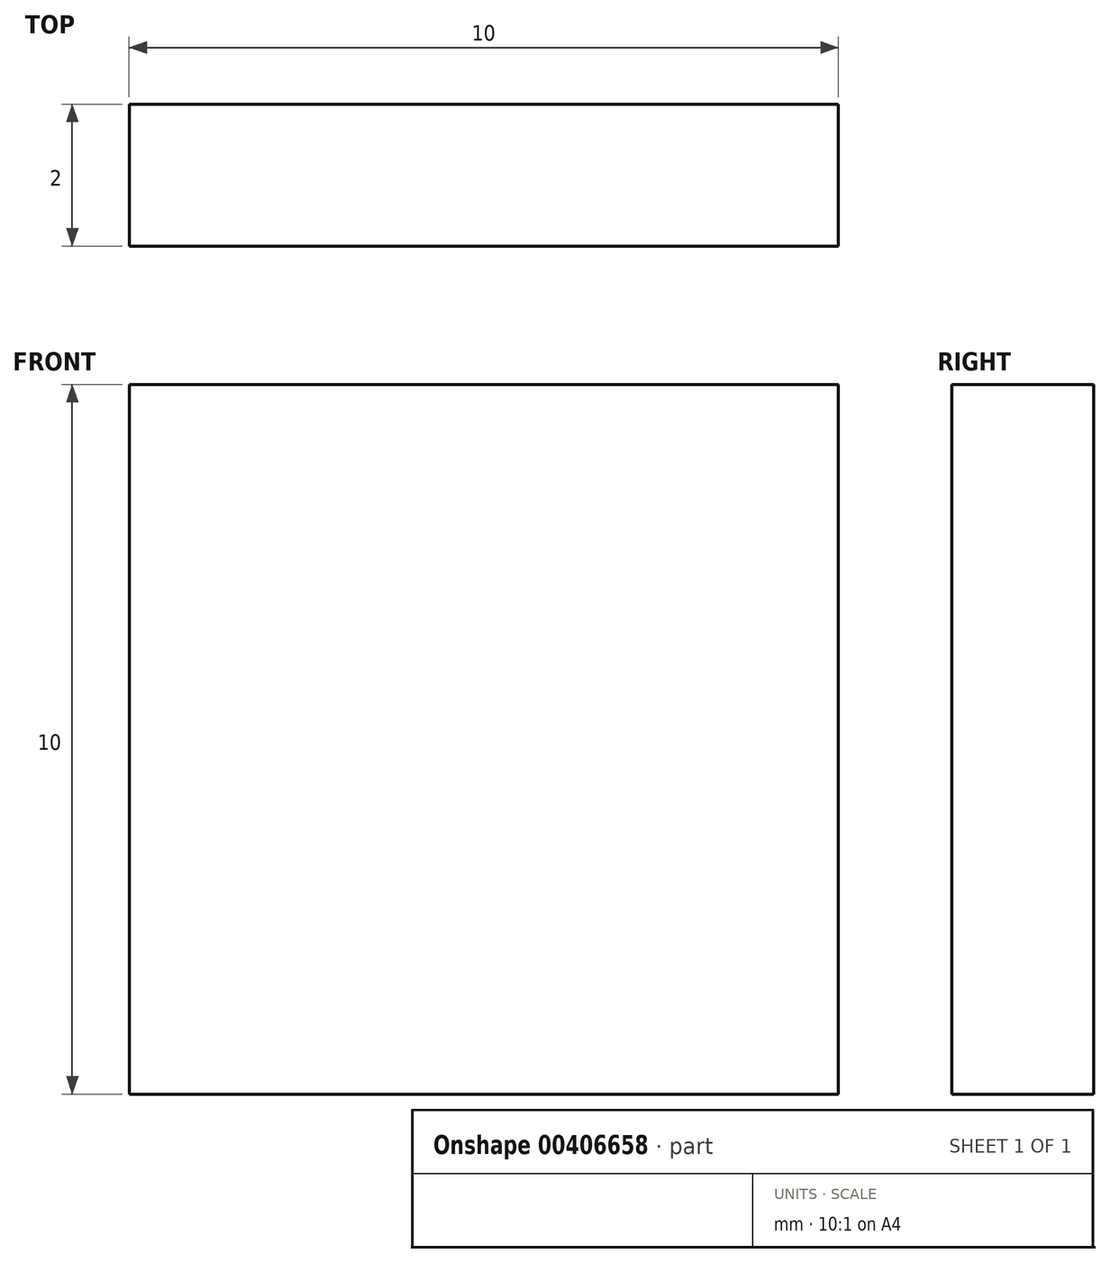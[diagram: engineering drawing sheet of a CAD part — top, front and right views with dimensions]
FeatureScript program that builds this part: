
annotation { "Feature Type Name" : "Feature", "Feature Type Description" : "" }
export const myFeature = defineFeature(function(context is Context, id is Id, definition is map)
    precondition{}
    {
        {
            var Q0;
            Q0=qCreatedBy(makeId("Front.planeOp"),FACE);
            cPlane(context, id + "F0", {"entities" : qUnion([Q0]), "cplaneType" : CPlaneType.OFFSET, "offset" : 5 * mm, "width" : 150 * mm, "height" : 150 * mm});
        }
        {
            var Q0;
            Q0=qCreatedBy(id+"F0.planeOp",FACE);
            var sketch = newSketch(context, id + "F1", { "sketchPlane" : qUnion([Q0])});
            skLineSegment(sketch, "E0.bottom", {"start": v(2.57, 4.93) * mm, "end": v(-7.43, 4.93) * mm});
            skLineSegment(sketch, "E0.top", {"start": v(2.57, -5.07) * mm, "end": v(-7.43, -5.07) * mm});
            skLineSegment(sketch, "E0.left", {"start": v(2.57, 4.93) * mm, "end": v(2.57, -5.07) * mm});
            skLineSegment(sketch, "E0.right", {"start": v(-7.43, 4.93) * mm, "end": v(-7.43, -5.07) * mm});
            skSolve(sketch);
        }
        {
            var Q0;
            Q0 = qSketchRegion(id + "F1", true);
            extrude(context, id + "F2", {"entities" : qUnion([Q0]), "depth" : 2 * mm, "offsetDistance" : 25 * mm});
        }
    });
